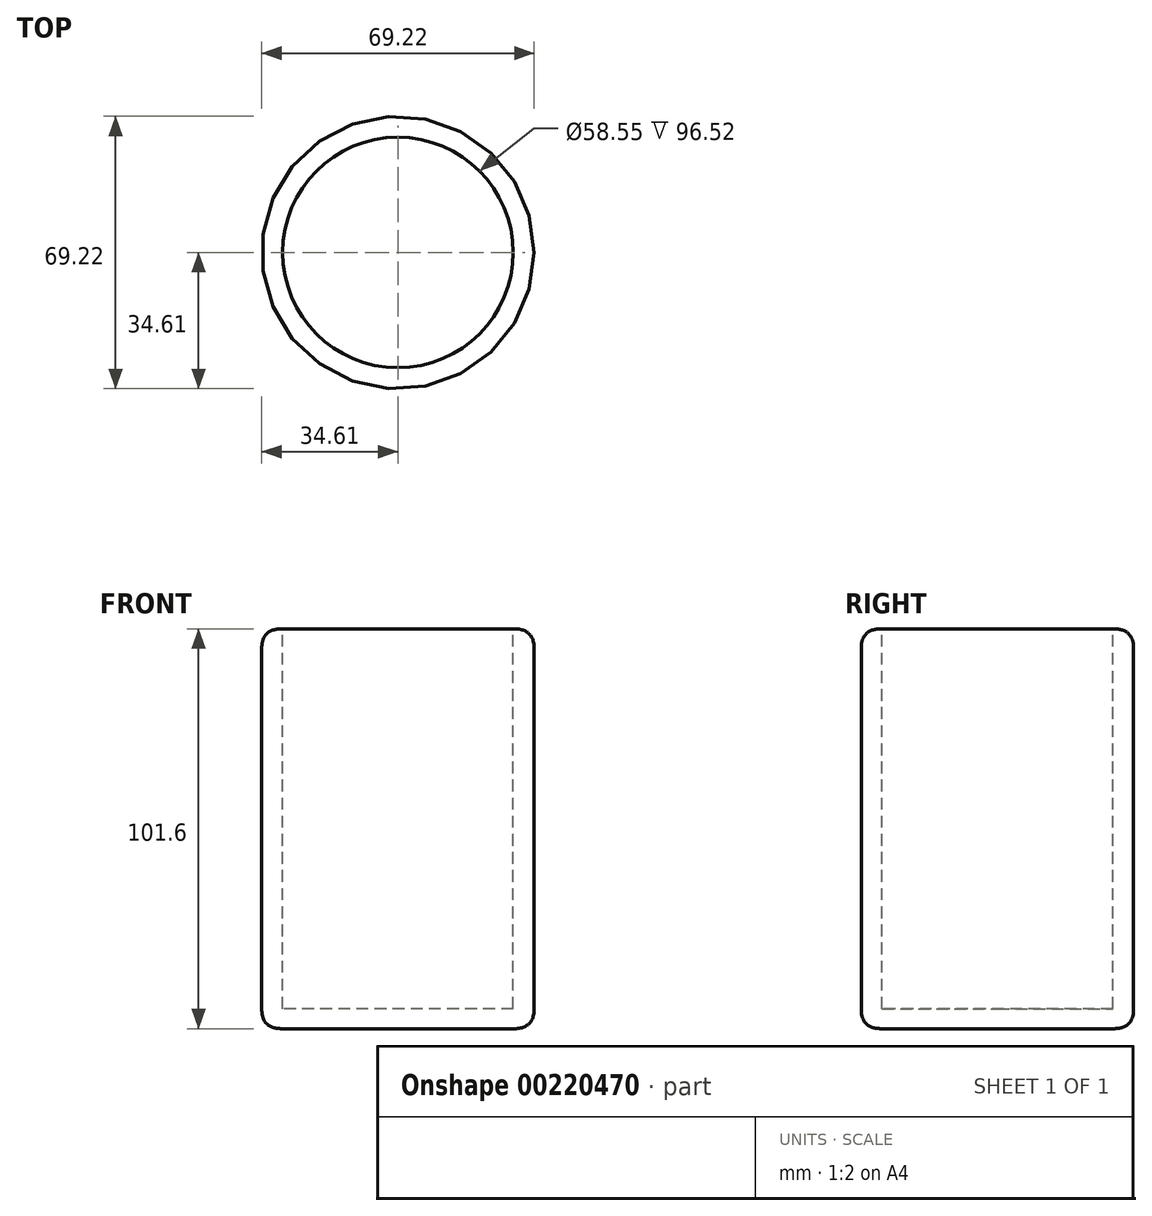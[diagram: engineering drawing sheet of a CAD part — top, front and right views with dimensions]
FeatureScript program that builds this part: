
annotation { "Feature Type Name" : "Feature", "Feature Type Description" : "" }
export const myFeature = defineFeature(function(context is Context, id is Id, definition is map)
    precondition{}
    {
        {
            var Q0;
            Q0=qCreatedBy(makeId("Top.planeOp"),FACE);
            var sketch = newSketch(context, id + "F0", { "sketchPlane" : qUnion([Q0])});
            skCircle(sketch, "E0", {"center": v(0, 0) * mm, "radius": 34.6 * mm});
            skSolve(sketch);
        }
        {
            var Q0;
            Q0 = qSketchRegion(id + "F0", true);
            extrude(context, id + "F1", {"entities" : qUnion([Q0]), "depth" : 101.6 * mm});
        }
        {
            var Q0;
            Q0=makeQuery(id+"F1.opExtrude","CAP_EDGE",EDGE,{"disambiguationData":[OSD([sQuery(id+"F0.wireOp",EDGE,"E0")])],"isStart":false});
            fillet(context, id + "F2", {"entities" : qUnion([Q0]), "radius" : 5.08 * mm, "rho" : .5, "crossSection" : FilletCrossSection.CONIC, "allowEdgeOverflow" : false});
        }
        {
            var Q0;
            Q0=makeQuery(id+"F1.opExtrude","CAP_EDGE",EDGE,{"disambiguationData":[OSD([sQuery(id+"F0.wireOp",EDGE,"E0")])],"isStart":true});
            fillet(context, id + "F3", {"entities" : qUnion([Q0]), "radius" : 5.08 * mm, "rho" : .5, "crossSection" : FilletCrossSection.CONIC, "allowEdgeOverflow" : false});
        }
        {
            var Q0;
            Q0=makeQuery(id+"F1.opExtrude","CAP_FACE",FACE,{"disambiguationData":[OSD([sQuery(id+"F0.wireOp",EDGE,"E0")])],"isStart":false});
            var sketch = newSketch(context, id + "F4", { "sketchPlane" : qUnion([Q0])});
            skCircle(sketch, "E1", {"center": v(0, 0) * mm, "radius": 29.27 * mm});
            skSolve(sketch);
        }
        {
            var Q0;
            Q0 = qSketchRegion(id + "F4", true);
            extrude(context, id + "F5", {"entities" : qUnion([Q0]), "operationType" : NewBodyOperationType.REMOVE, "oppositeDirection" : true, "depth" : 96.52 * mm});
        }
        {
            var Q0;
            Q0=qCreatedBy(makeId("Top.planeOp"),FACE);
            cPlane(context, id + "F6", {"entities" : qUnion([Q0]), "cplaneType" : CPlaneType.OFFSET, "offset" : 101.6 * mm, "width" : 152.4 * mm, "height" : 152.4 * mm});
        }
        {
            var Q0;
            Q0=qCreatedBy(id+"F6.planeOp",FACE);
            var sketch = newSketch(context, id + "F7", { "sketchPlane" : qUnion([Q0])});
            skCircle(sketch, "E2", {"center": v(0, 0) * mm, "radius": 29.23 * mm});
            skSolve(sketch);
        }
        {
            var Q0;
            Q0 = qSketchRegion(id + "F7", true);
            extrude(context, id + "F8", {"entities" : qUnion([Q0]), "operationType" : NewBodyOperationType.REMOVE, "oppositeDirection" : true, "depth" : 0.5 * mm});
        }
    });
